# Revit family: _Комплекс канат, кольца, шведская стенка, 3 турника и 2 наклонных скамьи Атлет
name_source: partatom
category: Антураж
revit_build: Autodesk Revit 2018 (Build: 20170927_1515(x64)
units: mm (PartAtom-declared; Revit-internal decimal feet)

## family parameters
Всегда вертикально = Да
Источник визуального образа = Геометрия семейства
На основе рабочей плоскости = Нет
Общий = Нет
При загрузке вырезать с полостями = Нет
Точка расчета площади = Нет

## types (1)
- Воркаут «Комплекс канат, кольца, шведская стенка, 3 турника и 2 наклонных скамьи Атлет»
    URL = https://hobbyka.ru
    Артикул товара = Арт. 40186
    Высота = 2650 мм
    Группа модели = Оборудование для воркаута
    Длина = 5248 мм
    Изготовитель = ООО «Хоббика»
    Изображение типоразмера = Комплекс канат, кольца, шведская стенка, 3 турника и 2 наклонных скамьи Атлет 001.png
    Материал изделия = сталь, канаты, дерево
    Описание = Воркаут «Комплекс канат, кольца, шведская стенка, 3 турника и 2 наклонных скамьи Атлет»
    Цвет каркаса = Сталь
    Ширина = 2730 мм
